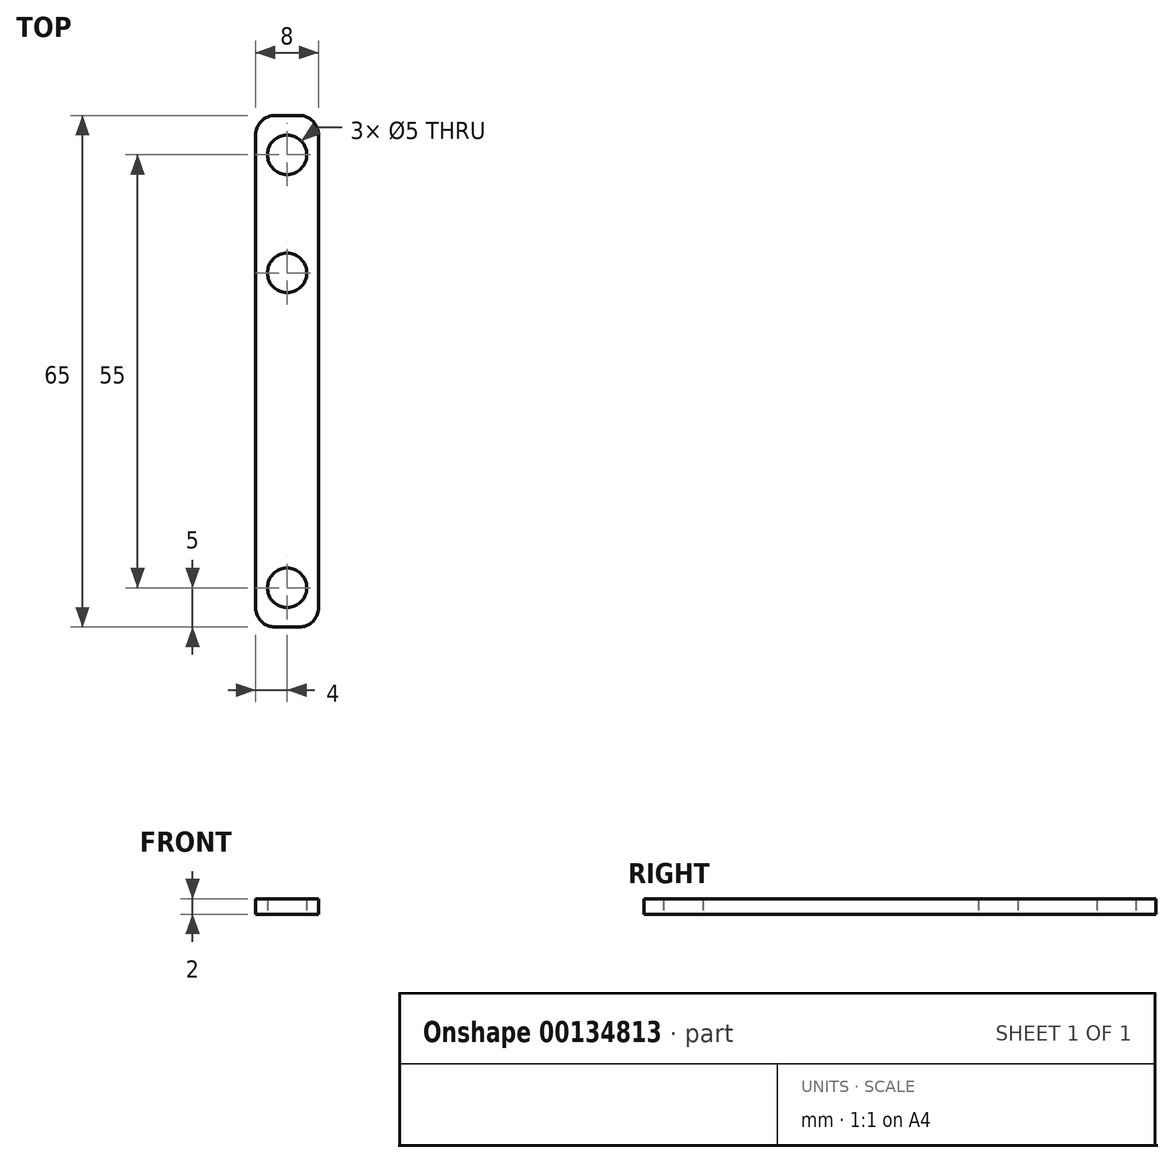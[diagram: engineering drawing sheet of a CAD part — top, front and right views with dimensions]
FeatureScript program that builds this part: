
annotation { "Feature Type Name" : "Feature", "Feature Type Description" : "" }
export const myFeature = defineFeature(function(context is Context, id is Id, definition is map)
    precondition{}
    {
        {
            var Q0;
            Q0=qCreatedBy(makeId("Top.planeOp"),FACE);
            var sketch = newSketch(context, id + "F0", { "sketchPlane" : qUnion([Q0])});
            skLineSegment(sketch, "E0.bottom", {"start": v(2.5, 0) * mm, "end": v(5.5, 0) * mm});
            skLineSegment(sketch, "E0.top", {"start": v(2.5, 65) * mm, "end": v(5.5, 65) * mm});
            skLineSegment(sketch, "E0.left", {"start": v(0, 2.5) * mm, "end": v(0, 62.5) * mm});
            skLineSegment(sketch, "E0.right", {"start": v(8, 2.5) * mm, "end": v(8, 62.5) * mm});
            skPoint(sketch, "E1", {"position": v(4, 65) * mm});
            skPoint(sketch, "E2", {"position": v(4, 0) * mm});
            skLineSegment(sketch, "E3", {"start": v(4, 65) * mm, "end": v(4, 0) * mm, "construction": true});
            skCircle(sketch, "E4", {"center": v(4, 60) * mm, "radius": 2.5 * mm});
            skCircle(sketch, "E5", {"center": v(4, 45) * mm, "radius": 2.5 * mm});
            skCircle(sketch, "E6", {"center": v(4, 5) * mm, "radius": 2.5 * mm});
            skPoint(sketch, "E7.visualSharp", {"position": v(0, 65) * mm});
            skArc(sketch, "E7.filletArc", {"start": v(2.5, 65) * mm, "mid": v(0.73, 64.27) * mm, "end": v(0, 62.5) * mm});
            skPoint(sketch, "E8.visualSharp", {"position": v(8, 65) * mm});
            skArc(sketch, "E8.filletArc", {"start": v(8, 62.5) * mm, "mid": v(7.27, 64.27) * mm, "end": v(5.5, 65) * mm});
            skPoint(sketch, "E9.visualSharp", {"position": v(8, 0) * mm});
            skArc(sketch, "E9.filletArc", {"start": v(5.5, 0) * mm, "mid": v(7.27, 0.73) * mm, "end": v(8, 2.5) * mm});
            skPoint(sketch, "E10.visualSharp", {"position": v(0, 0) * mm});
            skArc(sketch, "E10.filletArc", {"start": v(0, 2.5) * mm, "mid": v(0.73, 0.73) * mm, "end": v(2.5, 0) * mm});
            skSolve(sketch);
        }
        {
            var Q0;
            Q0=makeQuery(id+"F0.imprint","IMPRINT",FACE,{"disambiguationData":[TD([[makeQuery(id+"F0.imprint","IMPRINT",EDGE,{"derivedFrom":sQuery(id+"F0.wireOp",EDGE,"E0.bottom")}),1.0]])]});
            extrude(context, id + "F1", {"entities" : qUnion([Q0]), "depth" : 2 * mm, "offsetDistance" : 25 * mm});
        }
    });
